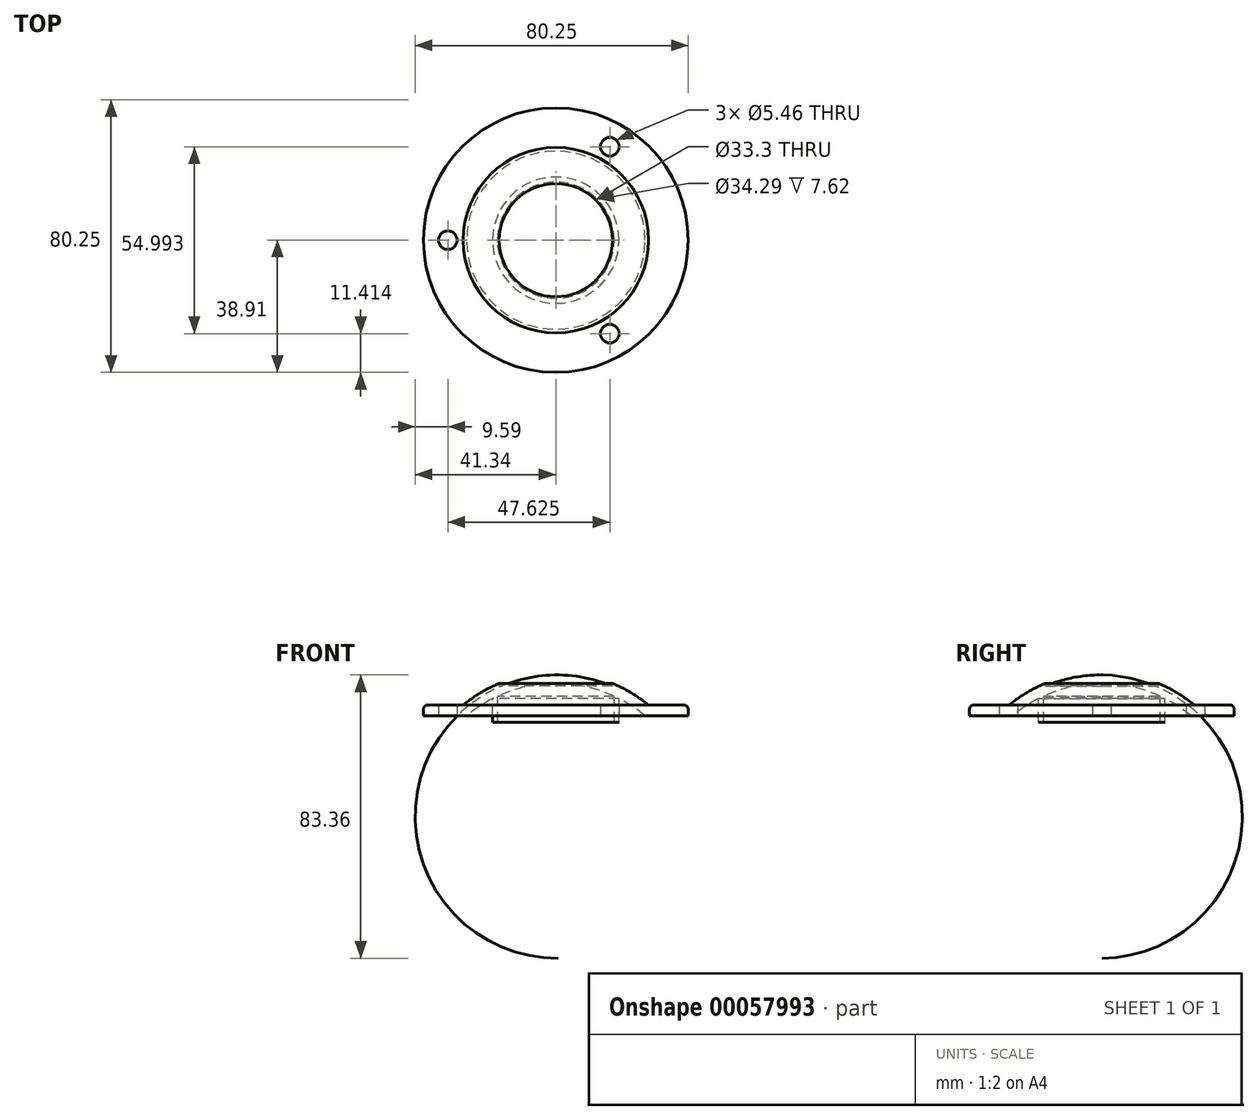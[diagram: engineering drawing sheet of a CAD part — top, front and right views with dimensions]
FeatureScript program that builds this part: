
annotation { "Feature Type Name" : "Feature", "Feature Type Description" : "" }
export const myFeature = defineFeature(function(context is Context, id is Id, definition is map)
    precondition{}
    {
        {
            var Q0;
            Q0=qCreatedBy(makeId("Front.planeOp"),FACE);
            var sketch = newSketch(context, id + "F0", { "sketchPlane" : qUnion([Q0])});
            skLineSegment(sketch, "E0", {"start": v(18.59, 0) * mm, "end": v(18.6, 0) * mm});
            skLineSegment(sketch, "E1", {"start": v(26.21, 1.59) * mm, "end": v(38.91, 1.59) * mm});
            skLineSegment(sketch, "E2", {"start": v(38.91, 1.59) * mm, "end": v(38.91, 3.5) * mm});
            skLineSegment(sketch, "E3", {"start": v(37.64, 4.76) * mm, "end": v(27.72, 4.76) * mm});
            skArc(sketch, "E4", {"start": v(21.87, 4.76) * mm, "mid": v(20.25, 5.74) * mm, "end": v(18.6, 6.63) * mm});
            skArc(sketch, "E5.trimOffspring", {"start": v(12.02, 9.3) * mm, "mid": v(6.08, 10.66) * mm, "end": v(0, 11.11) * mm});
            skArc(sketch, "E6.trimOffspring", {"start": v(26.21, 1.59) * mm, "mid": v(24.1, 3.25) * mm, "end": v(21.87, 4.76) * mm});
            skPoint(sketch, "E7.orphan", {"position": v(23.05, 1.59) * mm});
            skArc(sketch, "E8.trimOffspring", {"start": v(17.15, 7.34) * mm, "mid": v(14.62, 8.4) * mm, "end": v(12.02, 9.3) * mm});
            skLineSegment(sketch, "E9", {"start": v(27.72, 4.76) * mm, "end": v(27.26, 4.76) * mm});
            skArc(sketch, "E10", {"start": v(16.65, 10.3) * mm, "mid": v(8.5, 12.81) * mm, "end": v(0, 13.62) * mm});
            skPoint(sketch, "E11.visualSharp", {"position": v(38.91, 4.76) * mm});
            skArc(sketch, "E11.filletArc", {"start": v(38.91, 3.5) * mm, "mid": v(38.54, 4.4) * mm, "end": v(37.64, 4.76) * mm});
            skLineSegment(sketch, "E12", {"start": v(0, 13.62) * mm, "end": v(0, 11.11) * mm});
            skLineSegment(sketch, "E13", {"start": v(17.15, 7.34) * mm, "end": v(17.15, -0.28) * mm});
            skLineSegment(sketch, "E14", {"start": v(17.15, -0.28) * mm, "end": v(18.59, -0.28) * mm});
            skPoint(sketch, "E15.start.orphan", {"position": v(17.15, 0) * mm});
            skLineSegment(sketch, "E16", {"start": v(18.59, -0.28) * mm, "end": v(18.6, 6.63) * mm});
            skArc(sketch, "E17.0", {"start": v(26.5, 5.36) * mm, "mid": v(21.77, 8.57) * mm, "end": v(16.65, 11.12) * mm});
            skLineSegment(sketch, "E18", {"start": v(16.65, 11.12) * mm, "end": v(16.65, 10.3) * mm});
            skLineSegment(sketch, "E19", {"start": v(26.5, 5.36) * mm, "end": v(27.26, 4.76) * mm});
            skSolve(sketch);
        }
        {
            var Q0;
            Q0=makeQuery(id+"F0.imprint","IMPRINT",FACE,{"disambiguationData":[TD([[makeQuery(id+"F0.imprint","IMPRINT",EDGE,{"derivedFrom":sQuery(id+"F0.wireOp",EDGE,"E1")}),1.0]])]});
            var Q1;
            Q1=sQuery(id+"F0.wireOp",EDGE,"E12");
            revolve(context, id + "F1", {"entities" : qUnion([Q0]), "axis" : qUnion([Q1]), "revolveType" : RevolveType.FULL});
        }
        {
            var Q0;
            Q0=qCreatedBy(makeId("Top.planeOp"),FACE);
            var sketch = newSketch(context, id + "F2", { "sketchPlane" : qUnion([Q0])});
            skCircle(sketch, "E20", {"center": v(-31.75, 0) * mm, "radius": 2.73 * mm});
            skCircle(sketch, "E21.1.0", {"center": v(15.87, -27.5) * mm, "radius": 2.73 * mm});
            skCircle(sketch, "E21.2.0", {"center": v(15.88, 27.5) * mm, "radius": 2.73 * mm});
            skPoint(sketch, "E21.center", {"position": v(0, 0) * mm});
            skSolve(sketch);
        }
        {
            var Q0;
            Q0=makeQuery(id+"F2.imprint","IMPRINT",FACE,{"disambiguationData":[TD([[makeQuery(id+"F2.imprint","IMPRINT",EDGE,{"derivedFrom":sQuery(id+"F2.wireOp",EDGE,"E20")}),1.0]])]});
            var Q1;
            Q1=makeQuery(id+"F2.imprint","IMPRINT",FACE,{"disambiguationData":[TD([[makeQuery(id+"F2.imprint","IMPRINT",EDGE,{"derivedFrom":sQuery(id+"F2.wireOp",EDGE,"E21.1.0")}),1.0]])]});
            var Q2;
            Q2=makeQuery(id+"F2.imprint","IMPRINT",FACE,{"disambiguationData":[TD([[makeQuery(id+"F2.imprint","IMPRINT",EDGE,{"derivedFrom":sQuery(id+"F2.wireOp",EDGE,"E21.2.0")}),1.0]])]});
            extrude(context, id + "F3", {"entities" : qUnion([Q0, Q1, Q2]), "operationType" : NewBodyOperationType.REMOVE, "endBound" : BoundingType.THROUGH_ALL, "depth" : 25.4 * mm});
        }
        {
            var Q0;
            Q0 = qSketchRegion(id + "F2", true);
            var Q1;
            Q1 = qConstructionFilter(qBodyType(qCreatedBy(id + "FhG2IRNmcVO8lkk_1" ,EDGE), BodyType.WIRE), ConstructionObject.NO);
            var Q2;
            Q2=makeQuery(id+"F1.opRevolve","SWEPT_BODY",BODY,{"disambiguationData":[OSD([sQuery(id+"F0.wireOp",EDGE,"E1"),sQuery(id+"F0.wireOp",EDGE,"E2"),sQuery(id+"F0.wireOp",EDGE,"E3"),sQuery(id+"F0.wireOp",EDGE,"E4"),sQuery(id+"F0.wireOp",EDGE,"E5.trimOffspring"),sQuery(id+"F0.wireOp",EDGE,"E6.trimOffspring"),sQuery(id+"F0.wireOp",EDGE,"E8.trimOffspring"),sQuery(id+"F0.wireOp",EDGE,"E9"),sQuery(id+"F0.wireOp",EDGE,"E10"),sQuery(id+"F0.wireOp",EDGE,"E11.filletArc"),sQuery(id+"F0.wireOp",EDGE,"E12"),sQuery(id+"F0.wireOp",EDGE,"E13"),sQuery(id+"F0.wireOp",EDGE,"E14"),sQuery(id+"F0.wireOp",EDGE,"E16"),sQuery(id+"F0.wireOp",EDGE,"E17.0"),sQuery(id+"F0.wireOp",EDGE,"E18"),sQuery(id+"F0.wireOp",EDGE,"E19")])]});
            extrude(context, id + "F4", {"entities" : qUnion([Q0]), "operationType" : NewBodyOperationType.REMOVE, "surfaceEntities" : qUnion([Q1]), "endBoundEntityBody" : qUnion([Q2]), "depth" : 25.4 * mm});
        }
    });
